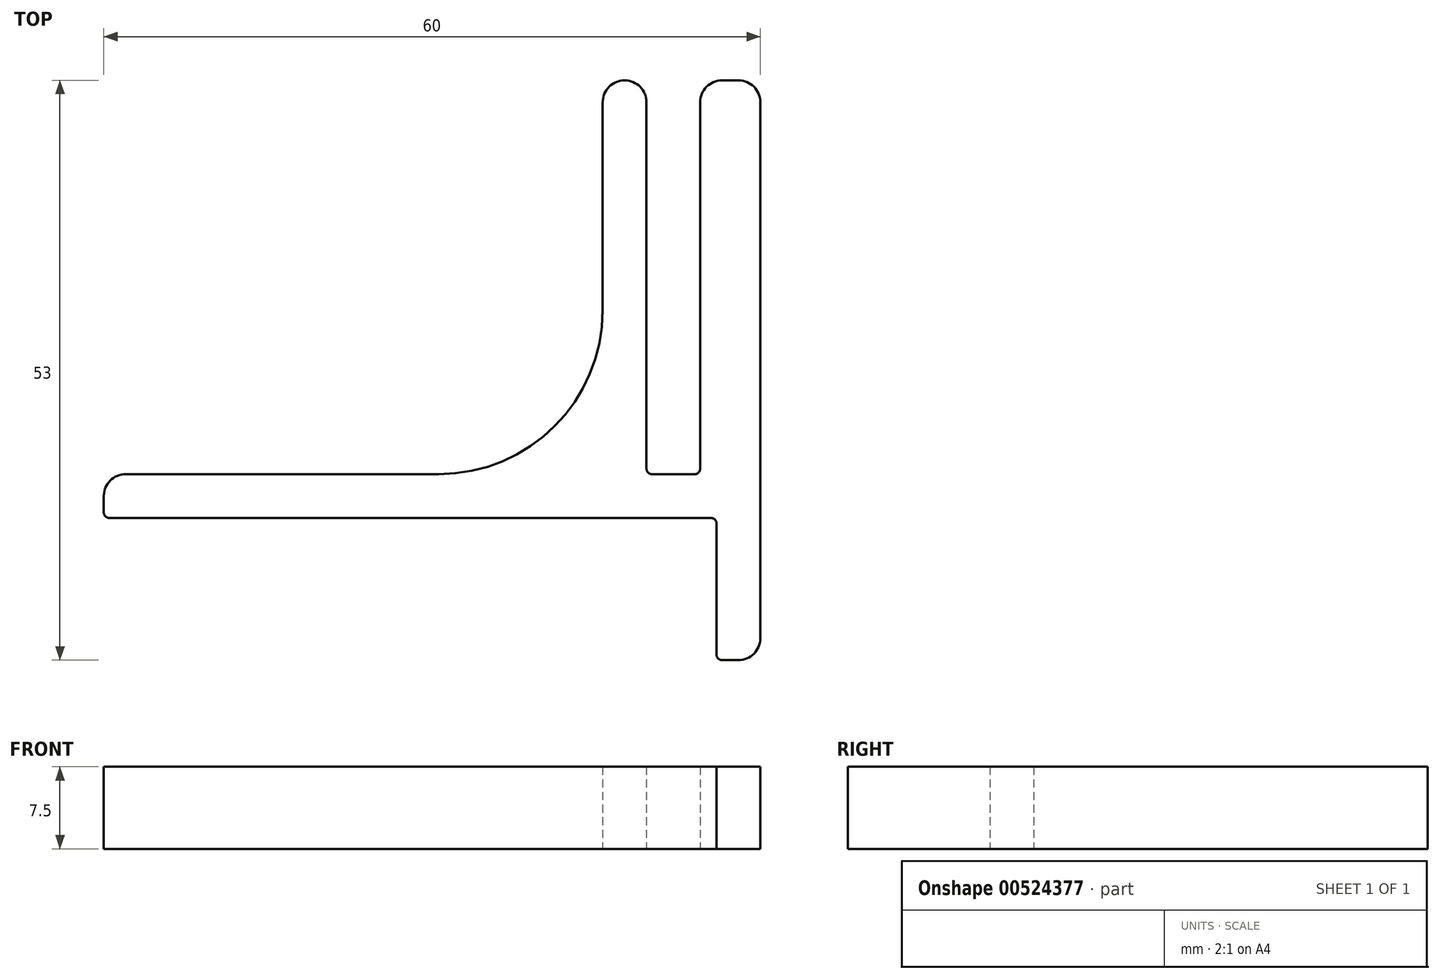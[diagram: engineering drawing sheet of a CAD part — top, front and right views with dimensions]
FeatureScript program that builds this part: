
annotation { "Feature Type Name" : "Feature", "Feature Type Description" : "" }
export const myFeature = defineFeature(function(context is Context, id is Id, definition is map)
    precondition{}
    {
        {
            var Q0;
            Q0=qCreatedBy(makeId("Top.planeOp"),FACE);
            var sketch = newSketch(context, id + "F0", { "sketchPlane" : qUnion([Q0])});
            skLineSegment(sketch, "E0", {"start": v(0, 4) * mm, "end": v(0, 0) * mm});
            skLineSegment(sketch, "E1", {"start": v(0, 0) * mm, "end": v(56, 0) * mm});
            skLineSegment(sketch, "E2", {"start": v(56, 0) * mm, "end": v(56, -13) * mm});
            skLineSegment(sketch, "E3", {"start": v(56, -13) * mm, "end": v(60, -13) * mm});
            skLineSegment(sketch, "E4", {"start": v(60, -13) * mm, "end": v(60, 40) * mm});
            skLineSegment(sketch, "E5", {"start": v(60, 40) * mm, "end": v(54.5, 40) * mm});
            skLineSegment(sketch, "E6", {"start": v(54.5, 40) * mm, "end": v(54.5, 4) * mm});
            skLineSegment(sketch, "E7", {"start": v(54.5, 4) * mm, "end": v(49.6, 4) * mm});
            skLineSegment(sketch, "E8", {"start": v(49.6, 4) * mm, "end": v(49.6, 40) * mm});
            skLineSegment(sketch, "E9", {"start": v(49.6, 40) * mm, "end": v(45.6, 40) * mm});
            skLineSegment(sketch, "E10", {"start": v(45.6, 40) * mm, "end": v(45.6, 4) * mm});
            skLineSegment(sketch, "E11", {"start": v(45.6, 4) * mm, "end": v(0, 4) * mm});
            skSolve(sketch);
        }
        {
            var Q0;
            Q0 = qSketchRegion(id + "F0", true);
            extrude(context, id + "F1", {"entities" : qUnion([Q0]), "depth" : 7.5 * mm, "offsetDistance" : 25 * mm});
        }
        {
            var Q0;
            Q0=makeQuery(id+"F1.opExtrude","SWEPT_EDGE",EDGE,{"disambiguationData":[OSD([sQuery(id+"F0.wireOp",EDGE,"E3"),sQuery(id+"F0.wireOp",EDGE,"E4")])]});
            var Q1;
            Q1=makeQuery(id+"F1.opExtrude","SWEPT_EDGE",EDGE,{"disambiguationData":[OSD([sQuery(id+"F0.wireOp",EDGE,"E4"),sQuery(id+"F0.wireOp",EDGE,"E5")])]});
            var Q2;
            Q2=makeQuery(id+"F1.opExtrude","SWEPT_EDGE",EDGE,{"disambiguationData":[OSD([sQuery(id+"F0.wireOp",EDGE,"E5"),sQuery(id+"F0.wireOp",EDGE,"E6")])]});
            var Q3;
            Q3=makeQuery(id+"F1.opExtrude","SWEPT_EDGE",EDGE,{"disambiguationData":[OSD([sQuery(id+"F0.wireOp",EDGE,"E8"),sQuery(id+"F0.wireOp",EDGE,"E9")])]});
            var Q4;
            Q4=makeQuery(id+"F1.opExtrude","SWEPT_EDGE",EDGE,{"disambiguationData":[OSD([sQuery(id+"F0.wireOp",EDGE,"E9"),sQuery(id+"F0.wireOp",EDGE,"E10")])]});
            var Q5;
            Q5=makeQuery(id+"F1.opExtrude","SWEPT_EDGE",EDGE,{"disambiguationData":[OSD([sQuery(id+"F0.wireOp",EDGE,"E0"),sQuery(id+"F0.wireOp",EDGE,"E11")])]});
            fillet(context, id + "F2", {"entities" : qUnion([Q0, Q1, Q2, Q3, Q4, Q5]), "radius" : 2 * mm, "tangentPropagation" : true, "allowEdgeOverflow" : false});
        }
        {
            var Q0;
            Q0=makeQuery(id+"F1.opExtrude","SWEPT_EDGE",EDGE,{"disambiguationData":[OSD([sQuery(id+"F0.wireOp",EDGE,"E10"),sQuery(id+"F0.wireOp",EDGE,"E11")])]});
            fillet(context, id + "F3", {"entities" : qUnion([Q0]), "radius" : 15 * mm, "tangentPropagation" : true, "allowEdgeOverflow" : false});
        }
        {
            var Q0;
            Q0=makeQuery(id+"F1.opExtrude","SWEPT_EDGE",EDGE,{"disambiguationData":[OSD([sQuery(id+"F0.wireOp",EDGE,"E7"),sQuery(id+"F0.wireOp",EDGE,"E8")])]});
            var Q1;
            Q1=makeQuery(id+"F1.opExtrude","SWEPT_EDGE",EDGE,{"disambiguationData":[OSD([sQuery(id+"F0.wireOp",EDGE,"E6"),sQuery(id+"F0.wireOp",EDGE,"E7")])]});
            var Q2;
            Q2=makeQuery(id+"F1.opExtrude","SWEPT_EDGE",EDGE,{"disambiguationData":[OSD([sQuery(id+"F0.wireOp",EDGE,"E0"),sQuery(id+"F0.wireOp",EDGE,"E1")])]});
            var Q3;
            Q3=makeQuery(id+"F1.opExtrude","SWEPT_EDGE",EDGE,{"disambiguationData":[OSD([sQuery(id+"F0.wireOp",EDGE,"E2"),sQuery(id+"F0.wireOp",EDGE,"E3")])]});
            var Q4;
            Q4=makeQuery(id+"F1.opExtrude","SWEPT_EDGE",EDGE,{"disambiguationData":[OSD([sQuery(id+"F0.wireOp",EDGE,"E1"),sQuery(id+"F0.wireOp",EDGE,"E2")])]});
            fillet(context, id + "F4", {"entities" : qUnion([Q0, Q1, Q2, Q3, Q4]), "radius" : 0.5 * mm, "tangentPropagation" : true, "allowEdgeOverflow" : false});
        }
    });
